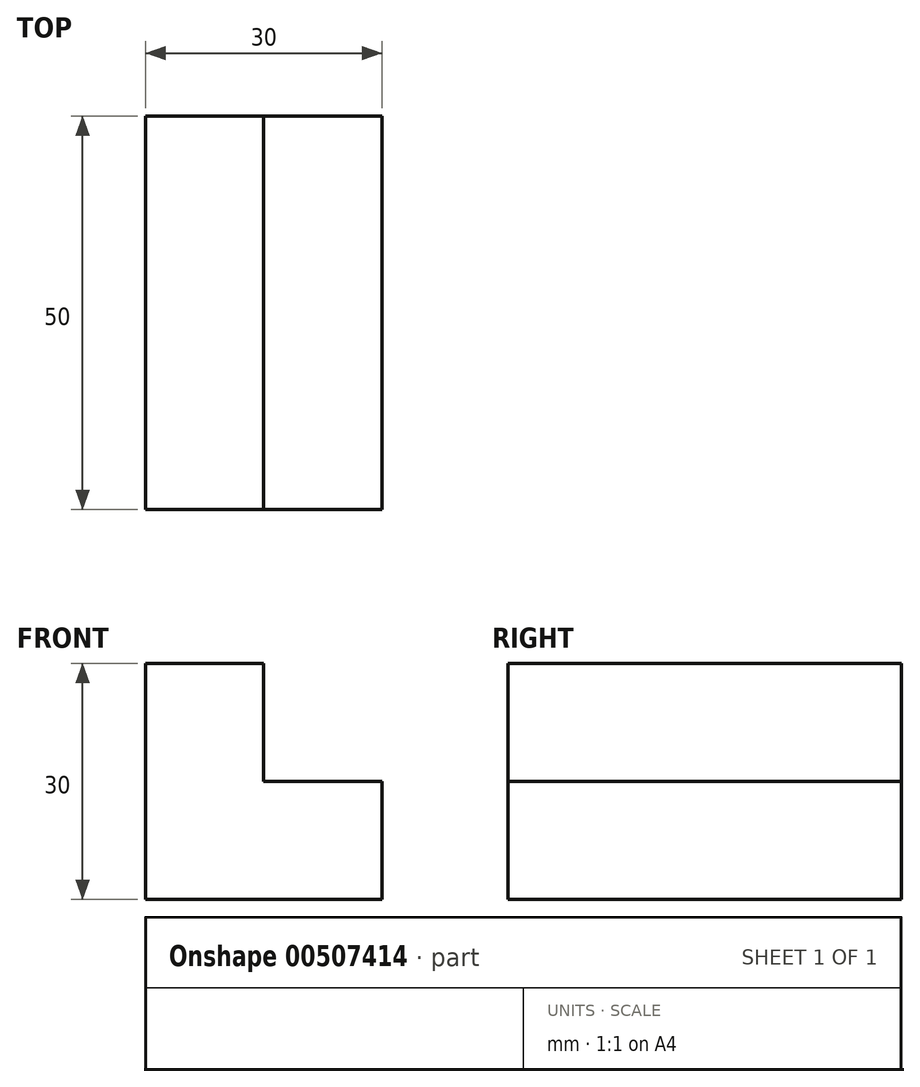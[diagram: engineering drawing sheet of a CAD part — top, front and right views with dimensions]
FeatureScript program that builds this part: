
annotation { "Feature Type Name" : "Feature", "Feature Type Description" : "" }
export const myFeature = defineFeature(function(context is Context, id is Id, definition is map)
    precondition{}
    {
        {
            var Q0;
            Q0=qCreatedBy(makeId("Front.planeOp"),FACE);
            var sketch = newSketch(context, id + "F0", { "sketchPlane" : qUnion([Q0])});
            skLineSegment(sketch, "E0", {"start": v(0, 0) * mm, "end": v(0, 30) * mm});
            skLineSegment(sketch, "E1", {"start": v(0, 30) * mm, "end": v(15, 30) * mm});
            skLineSegment(sketch, "E2", {"start": v(15, 30) * mm, "end": v(15, 15) * mm});
            skLineSegment(sketch, "E3", {"start": v(15, 15) * mm, "end": v(30, 15) * mm});
            skLineSegment(sketch, "E4", {"start": v(30, 15) * mm, "end": v(30, 0) * mm});
            skLineSegment(sketch, "E5", {"start": v(30, 0) * mm, "end": v(0, 0) * mm});
            skSolve(sketch);
        }
        {
            var Q0;
            Q0=makeQuery(id+"F0.imprint","IMPRINT",FACE,{"disambiguationData":[TD([[makeQuery(id+"F0.imprint","IMPRINT",EDGE,{"derivedFrom":sQuery(id+"F0.wireOp",EDGE,"E0")}),-1.0]])]});
            extrude(context, id + "F1", {"entities" : qUnion([Q0]), "depth" : 50 * mm});
        }
    });
